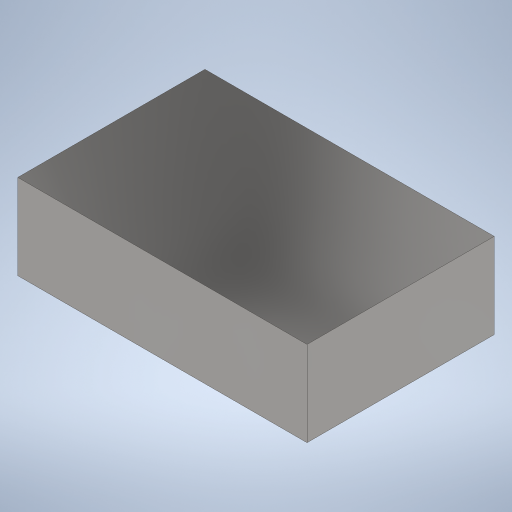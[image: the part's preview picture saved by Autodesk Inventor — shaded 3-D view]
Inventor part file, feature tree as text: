
AUTODESK INVENTOR PART (.ipt)
format: ipt  version: 2023 (Build 270158000, 158)  size: 204,800 bytes
history: native  units: in
note: dims shown in document units (in); Inventor stores cm internally (conversion verified against a paired STEP export)
features: extrude x1, sketch x1
ambient origin geometry x8: Origin, YZ Plane, XZ Plane, XY Plane, X Axis, Y Axis, Z Axis, Center Point
bodies: Solid1 (feature_tree)
feature tree (2):
  extrude  "Extrusion1"  Depth=3.3465in
  sketch  "Sketch1"  dims[d0=2.1654in d1=3.3465in d2=0.9843in d3=0.0in]
